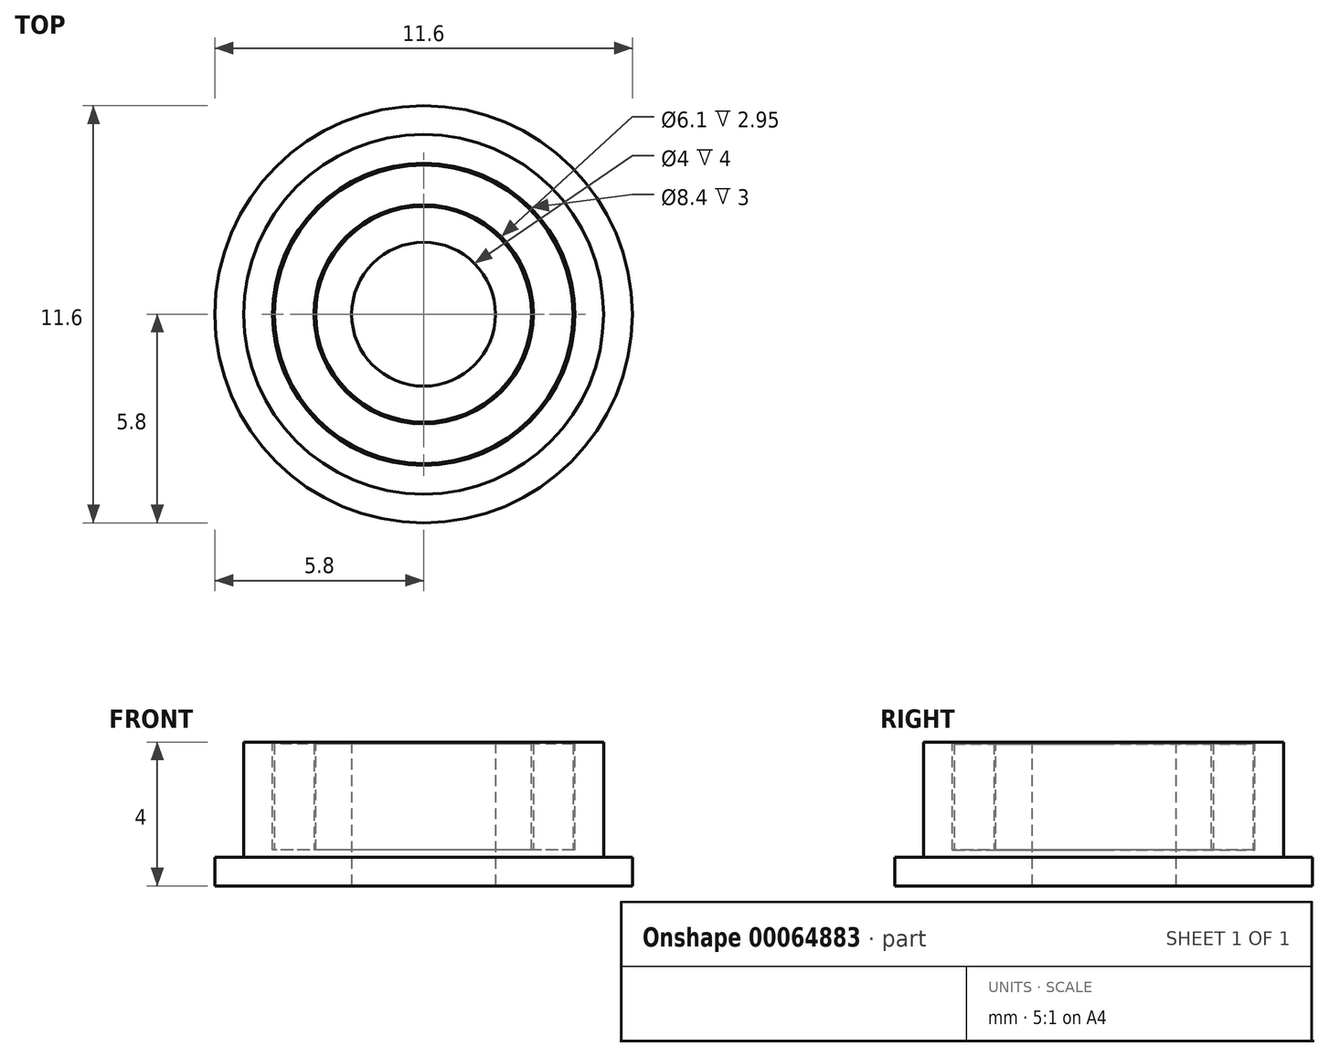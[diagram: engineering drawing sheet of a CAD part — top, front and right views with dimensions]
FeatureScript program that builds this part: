
annotation { "Feature Type Name" : "Feature", "Feature Type Description" : "" }
export const myFeature = defineFeature(function(context is Context, id is Id, definition is map)
    precondition{}
    {
        {
            var Q0;
            Q0=qCreatedBy(makeId("Front.planeOp"),FACE);
            var sketch = newSketch(context, id + "F0", { "sketchPlane" : qUnion([Q0])});
            skLineSegment(sketch, "E0.top", {"start": v(0, 4) * mm, "end": v(5, 4) * mm, "construction": true});
            skLineSegment(sketch, "E0.left", {"start": v(0, 0) * mm, "end": v(0, 4) * mm, "construction": true});
            skLineSegment(sketch, "E1", {"start": v(0, 0) * mm, "end": v(2, 0) * mm});
            skLineSegment(sketch, "E2", {"start": v(2, 0) * mm, "end": v(5.8, 0) * mm});
            skLineSegment(sketch, "E3", {"start": v(5.8, 0) * mm, "end": v(5.8, 0.8) * mm});
            skLineSegment(sketch, "E4", {"start": v(5.8, 0.8) * mm, "end": v(5, 0.8) * mm});
            skLineSegment(sketch, "E5", {"start": v(5, 0.8) * mm, "end": v(5, 4) * mm});
            skLineSegment(sketch, "E6", {"start": v(5, 4) * mm, "end": v(2, 4) * mm});
            skLineSegment(sketch, "E7", {"start": v(2, 4) * mm, "end": v(2, 0) * mm});
            skSolve(sketch);
        }
        {
            var Q0;
            Q0=makeQuery(id+"F0.imprint","IMPRINT",FACE,{"disambiguationData":[TD([[makeQuery(id+"F0.imprint","IMPRINT",EDGE,{"derivedFrom":sQuery(id+"F0.wireOp",EDGE,"E2")}),1.0]])]});
            var Q1;
            Q1=sQuery(id+"F0.wireOp",EDGE,"E0.left");
            revolve(context, id + "F1", {"entities" : qUnion([Q0]), "axis" : qUnion([Q1]), "revolveType" : RevolveType.FULL});
        }
        {
            var Q0;
            Q0=makeQuery(id+"F1.opRevolve","SWEPT_FACE",FACE,{"disambiguationData":[OSD([sQuery(id+"F0.wireOp",EDGE,"E6")])]});
            var sketch = newSketch(context, id + "F2", { "sketchPlane" : qUnion([Q0])});
            skCircle(sketch, "E8.0", {"center": v(0, 0) * mm, "radius": 4.2 * mm});
            skCircle(sketch, "E9.0", {"center": v(0, 0) * mm, "radius": 3 * mm});
            skSolve(sketch);
        }
        {
            var Q0;
            Q0=makeQuery(id+"F2.imprint","IMPRINT",FACE,{"disambiguationData":[TD([[makeQuery(id+"F2.imprint","IMPRINT",EDGE,{"derivedFrom":sQuery(id+"F2.wireOp",EDGE,"E8.0")}),1.0]])]});
            extrude(context, id + "F3", {"entities" : qUnion([Q0]), "operationType" : NewBodyOperationType.REMOVE, "oppositeDirection" : true, "depth" : 3 * mm});
        }
        {
            var Q0;
            Q0=makeQuery(id+"F3.boolean.opBoolean","COPY",FACE,{"derivedFrom":makeQuery(id+"F3.opExtrude","CAP_FACE",FACE,{"disambiguationData":[OSD([sQuery(id+"F2.wireOp",EDGE,"E8.0"),sQuery(id+"F2.wireOp",EDGE,"E9.0")])],"isStart":false})});
            var sketch = newSketch(context, id + "F4", { "sketchPlane" : qUnion([Q0])});
            skCircle(sketch, "E10.0", {"center": v(0, 0) * mm, "radius": 3.05 * mm});
            skCircle(sketch, "E11.0", {"center": v(0, 0) * mm, "radius": 4.15 * mm});
            skSolve(sketch);
        }
        {
            var Q0;
            Q0=makeQuery(id+"F4.imprint","IMPRINT",FACE,{"disambiguationData":[TD([[makeQuery(id+"F4.imprint","IMPRINT",EDGE,{"derivedFrom":sQuery(id+"F4.wireOp",EDGE,"E10.0")}),-1.0]])]});
            extrude(context, id + "F5", {"entities" : qUnion([Q0]), "depth" : 2.95 * mm});
        }
    });
